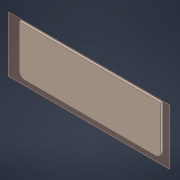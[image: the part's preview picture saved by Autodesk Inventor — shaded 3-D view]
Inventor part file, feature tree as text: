
AUTODESK INVENTOR PART (.ipt)
format: ipt  version: 2021 (Build 250183000, 183)  size: 97,792 bytes
history: native  units: mm
features: other x3, reference x2, plane x1, extrude x1, thicken_offset x1, sketch x1
ambient origin geometry x8: Origin, YZ Plane, XZ Plane, XY Plane, X Axis, Y Axis, Z Axis, Center Point
bodies: Solid1 (feature_tree)
feature tree (9):
  plane  "Work Plane1"
  extrude  "Extrusion1"  Depth=1.5mm
  thicken_offset  "Thicken1"
  sketch  "Sketch1"  dims[d0=1.5mm d1=0.0mm d2=0.1mm d3=0.1mm]
  reference  "Reference1"
  reference  "Reference2"
  parser-record x1  (decoder bookkeeping rows leaked as tree rows — omitted from the tree; the rows remain in map.json)
  other  "NEW_COVER_220DET_COMPLETE.iam"
  other  "NEW_COVER_220DET:1"
note: 1 file-system path scrubbed to <path> (originals preserved in map.json)
